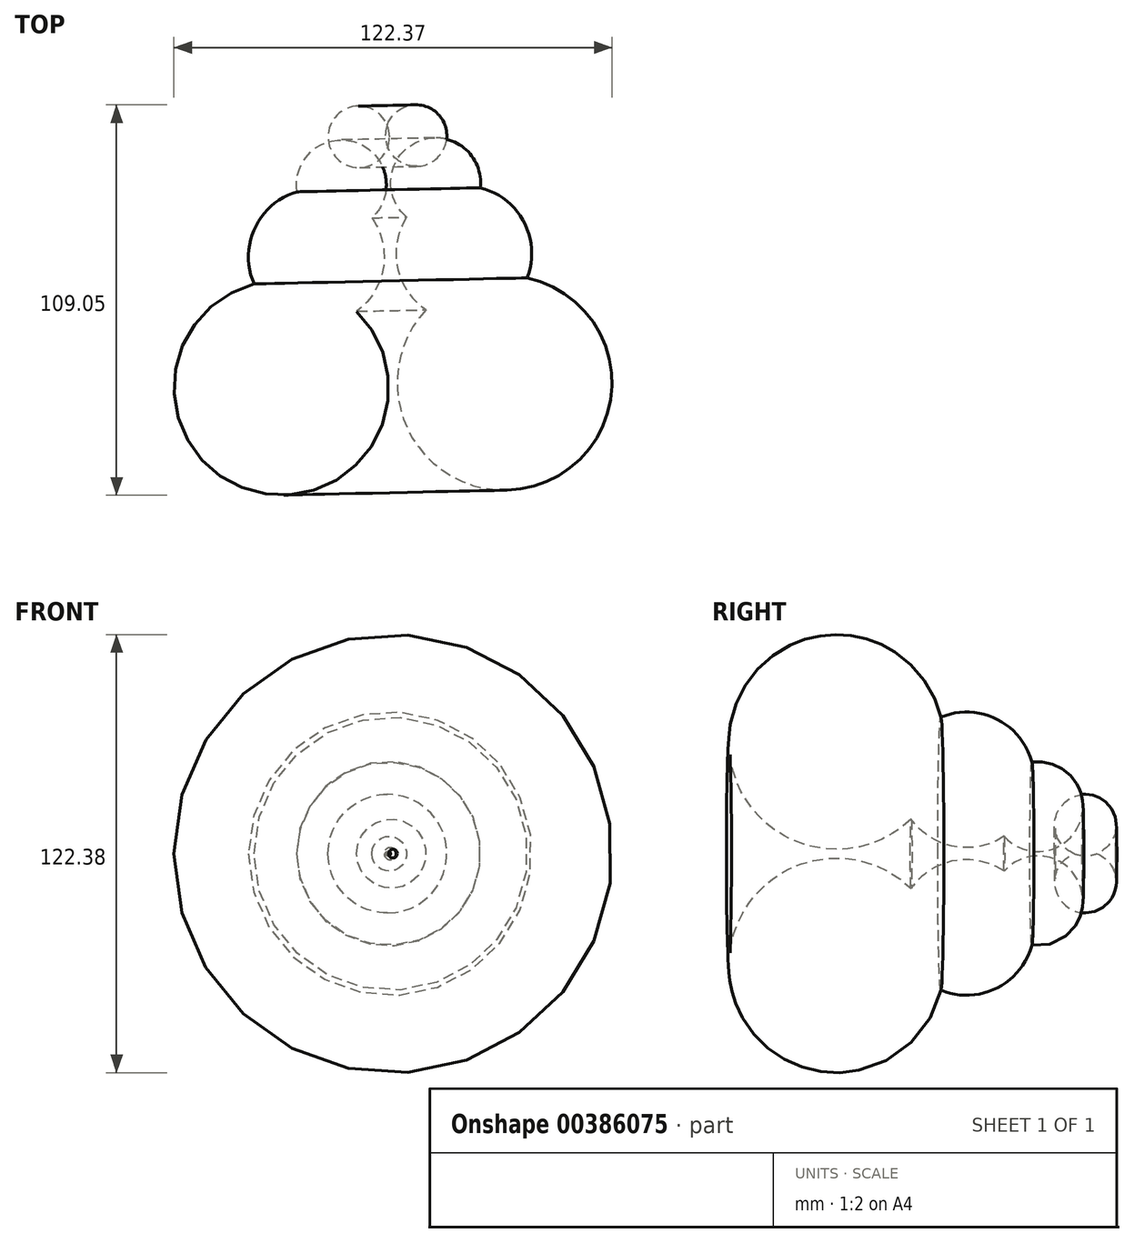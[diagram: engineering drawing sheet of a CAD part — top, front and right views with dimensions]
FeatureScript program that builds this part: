
annotation { "Feature Type Name" : "Feature", "Feature Type Description" : "" }
export const myFeature = defineFeature(function(context is Context, id is Id, definition is map)
    precondition{}
    {
        {
            var Q0;
            Q0=qCreatedBy(makeId("Top.planeOp"),FACE);
            var sketch = newSketch(context, id + "F0", { "sketchPlane" : qUnion([Q0])});
            skCircle(sketch, "E0", {"center": v(-23.64, 42.52) * mm, "radius": 8.59 * mm});
            skCircle(sketch, "E1", {"center": v(-28.5, 29.1) * mm, "radius": 12.55 * mm});
            skCircle(sketch, "E2", {"center": v(-35.5, 9) * mm, "radius": 18.95 * mm});
            skCircle(sketch, "E3", {"center": v(-45.29, -27.6) * mm, "radius": 30 * mm});
            skLineSegment(sketch, "E4", {"start": v(-15.9, 55.01) * mm, "end": v(-13.35, -60.5) * mm});
            skLineSegment(sketch, "E5", {"start": v(-31.73, -54.35) * mm, "end": v(-31.73, -73.91) * mm});
            skLineSegment(sketch, "E6", {"start": v(-31.73, -73.91) * mm, "end": v(-4.57, -73.91) * mm});
            skSolve(sketch);
        }
        {
            var Q0;
            {var subQ0=sQuery(id+"F0.wireOp",EDGE,"E3");var subQ4=makeQuery(id+"F0.imprint","IMPRINT",VERTEX,{"derivedFrom":subQ0});Q0=makeQuery(id+"F0.imprint","IMPRINT",FACE,{"disambiguationData":[TD([[makeQuery(id+"F0.imprint","IMPRINT",EDGE,{"disambiguationData":[TD([[subQ4,1.0]])],"derivedFrom":subQ0}),1.0]])]});}
            var Q1;
            {var subQ0=sQuery(id+"F0.wireOp",EDGE,"E3");var subQ1=sQuery(id+"F0.wireOp",EDGE,"E2");var subQ2=makeQuery(id+"F0.imprint","INTERSECT",VERTEX,{"disambiguationData":[OD(0.0)],"derivedFrom":[subQ1,subQ0]});Q1=makeQuery(id+"F0.imprint","IMPRINT",FACE,{"disambiguationData":[TD([[makeQuery(id+"F0.imprint","IMPRINT",EDGE,{"disambiguationData":[TD([[subQ2,-1.0]])],"derivedFrom":subQ1}),1.0]])]});}
            var Q2;
            {var subQ0=sQuery(id+"F0.wireOp",EDGE,"E2");var subQ1=sQuery(id+"F0.wireOp",EDGE,"E1");var subQ2=makeQuery(id+"F0.imprint","INTERSECT",VERTEX,{"disambiguationData":[OD(0.0)],"derivedFrom":[subQ1,subQ0]});Q2=makeQuery(id+"F0.imprint","IMPRINT",FACE,{"disambiguationData":[TD([[makeQuery(id+"F0.imprint","IMPRINT",EDGE,{"disambiguationData":[TD([[subQ2,-1.0]])],"derivedFrom":subQ1}),-1.0]])]});}
            var Q3;
            {var subQ0=sQuery(id+"F0.wireOp",EDGE,"E2");var subQ1=sQuery(id+"F0.wireOp",EDGE,"E1");var subQ2=makeQuery(id+"F0.imprint","INTERSECT",VERTEX,{"disambiguationData":[OD(0.0)],"derivedFrom":[subQ1,subQ0]});Q3=makeQuery(id+"F0.imprint","IMPRINT",FACE,{"disambiguationData":[TD([[makeQuery(id+"F0.imprint","IMPRINT",EDGE,{"disambiguationData":[TD([[subQ2,-1.0]])],"derivedFrom":subQ1}),1.0]])]});}
            var Q4;
            {var subQ0=sQuery(id+"F0.wireOp",EDGE,"E1");var subQ1=sQuery(id+"F0.wireOp",EDGE,"E0");var subQ2=makeQuery(id+"F0.imprint","INTERSECT",VERTEX,{"disambiguationData":[OD(0.0)],"derivedFrom":[subQ1,subQ0]});Q4=makeQuery(id+"F0.imprint","IMPRINT",FACE,{"disambiguationData":[TD([[makeQuery(id+"F0.imprint","IMPRINT",EDGE,{"disambiguationData":[TD([[subQ2,-1.0]])],"derivedFrom":subQ1}),-1.0]])]});}
            var Q5;
            {var subQ0=sQuery(id+"F0.wireOp",EDGE,"E4");var subQ1=sQuery(id+"F0.wireOp",EDGE,"E0");var subQ2=makeQuery(id+"F0.imprint","INTERSECT",VERTEX,{"disambiguationData":[OD(0.0)],"derivedFrom":[subQ1,subQ0]});Q5=makeQuery(id+"F0.imprint","IMPRINT",FACE,{"disambiguationData":[TD([[makeQuery(id+"F0.imprint","IMPRINT",EDGE,{"disambiguationData":[TD([[subQ2,-1.0]])],"derivedFrom":subQ1}),1.0]])]});}
            var Q6;
            {var subQ0=sQuery(id+"F0.wireOp",EDGE,"E1");var subQ1=sQuery(id+"F0.wireOp",EDGE,"E0");var subQ2=makeQuery(id+"F0.imprint","INTERSECT",VERTEX,{"disambiguationData":[OD(0.0)],"derivedFrom":[subQ1,subQ0]});Q6=makeQuery(id+"F0.imprint","IMPRINT",FACE,{"disambiguationData":[TD([[makeQuery(id+"F0.imprint","IMPRINT",EDGE,{"disambiguationData":[TD([[subQ2,-1.0]])],"derivedFrom":subQ1}),1.0]])]});}
            var Q7;
            Q7=sQuery(id+"F0.wireOp",EDGE,"E4");
            revolve(context, id + "F1", {"entities" : qUnion([Q0, Q1, Q2, Q3, Q4, Q5, Q6]), "axis" : qUnion([Q7]), "revolveType" : RevolveType.FULL});
        }
    });
